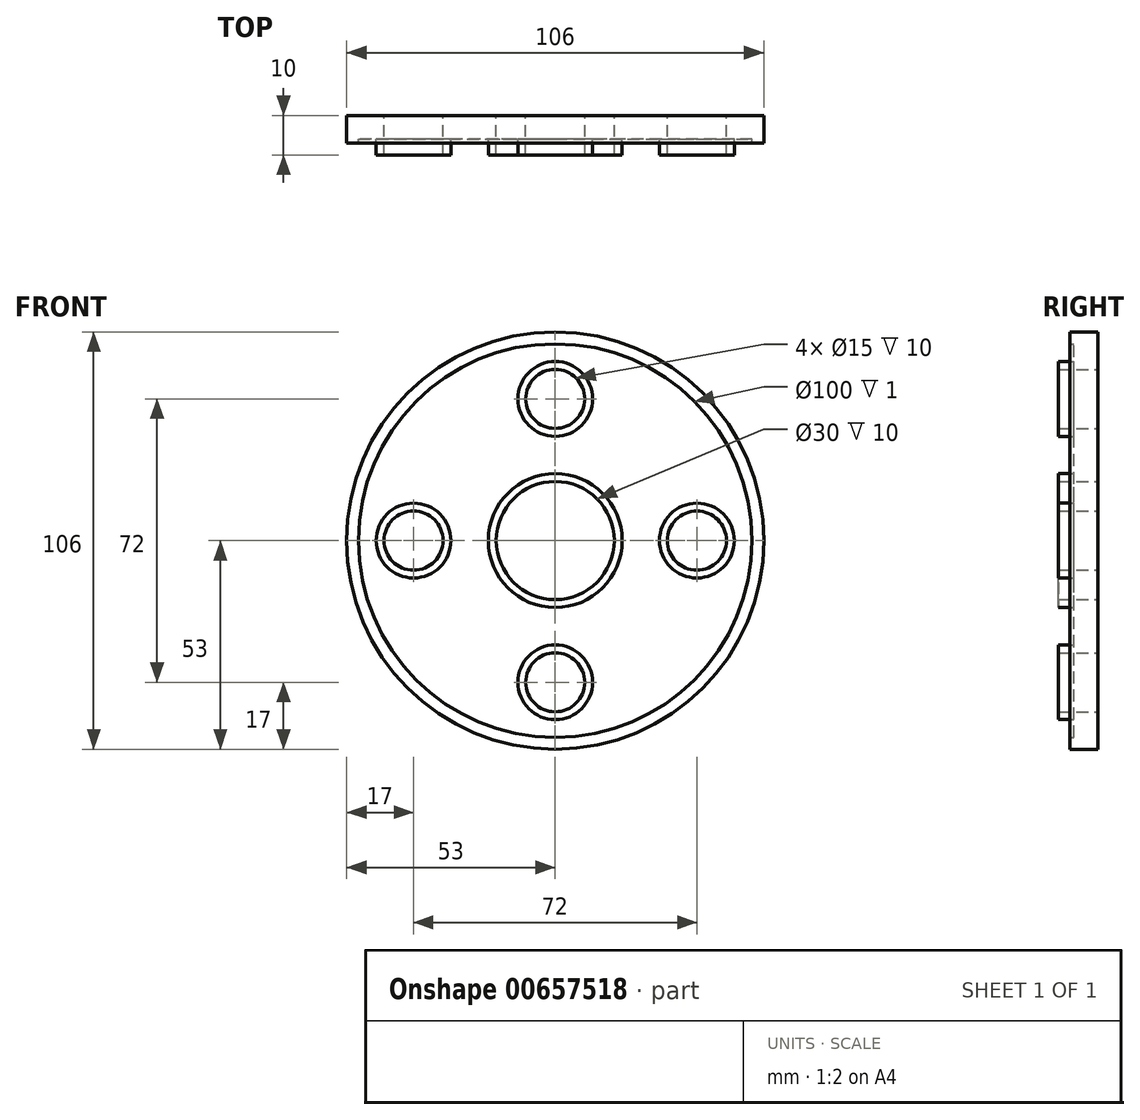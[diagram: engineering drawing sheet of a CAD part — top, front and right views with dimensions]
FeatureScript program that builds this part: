
annotation { "Feature Type Name" : "Feature", "Feature Type Description" : "" }
export const myFeature = defineFeature(function(context is Context, id is Id, definition is map)
    precondition{}
    {
        {
            var Q0;
            Q0=qCreatedBy(makeId("Front.planeOp"),FACE);
            var sketch = newSketch(context, id + "F0", { "sketchPlane" : qUnion([Q0])});
            skCircle(sketch, "E0", {"center": v(0, 0) * mm, "radius": 15 * mm});
            skCircle(sketch, "E1", {"center": v(0, 0) * mm, "radius": 50 * mm});
            skCircle(sketch, "E2", {"center": v(0, 0) * mm, "radius": 53 * mm});
            skCircle(sketch, "E3", {"center": v(0, 0) * mm, "radius": 17 * mm});
            skCircle(sketch, "E4", {"center": v(-36, 0) * mm, "radius": 7.5 * mm});
            skCircle(sketch, "E5", {"center": v(-36, 0) * mm, "radius": 9.5 * mm});
            skCircle(sketch, "E6.1.0", {"center": v(0, 36) * mm, "radius": 7.5 * mm});
            skCircle(sketch, "E6.1.1", {"center": v(0, 36) * mm, "radius": 9.5 * mm});
            skCircle(sketch, "E6.2.0", {"center": v(36, 0) * mm, "radius": 7.5 * mm});
            skCircle(sketch, "E6.2.1", {"center": v(36, 0) * mm, "radius": 9.5 * mm});
            skCircle(sketch, "E6.3.0", {"center": v(0, -36) * mm, "radius": 7.5 * mm});
            skCircle(sketch, "E6.3.1", {"center": v(0, -36) * mm, "radius": 9.5 * mm});
            skSolve(sketch);
        }
        {
            var Q0;
            Q0=makeQuery(id+"F0.imprint","IMPRINT",FACE,{"disambiguationData":[TD([[makeQuery(id+"F0.imprint","IMPRINT",EDGE,{"derivedFrom":sQuery(id+"F0.wireOp",EDGE,"E1")}),-1.0]])]});
            extrude(context, id + "F1", {"entities" : qUnion([Q0]), "depth" : 7 * mm, "offsetDistance" : 25 * mm});
        }
        {
            var Q0;
            Q0=makeQuery(id+"F0.imprint","IMPRINT",FACE,{"disambiguationData":[TD([[makeQuery(id+"F0.imprint","IMPRINT",EDGE,{"derivedFrom":sQuery(id+"F0.wireOp",EDGE,"E1")}),1.0]])]});
            extrude(context, id + "F2", {"entities" : qUnion([Q0]), "operationType" : NewBodyOperationType.ADD, "depth" : 6 * mm, "offsetDistance" : 25 * mm});
        }
        {
            var Q0;
            Q0=makeQuery(id+"F0.imprint","IMPRINT",FACE,{"disambiguationData":[TD([[makeQuery(id+"F0.imprint","IMPRINT",EDGE,{"derivedFrom":sQuery(id+"F0.wireOp",EDGE,"E6.2.0")}),-1.0]])]});
            extrude(context, id + "F3", {"entities" : qUnion([Q0]), "operationType" : NewBodyOperationType.ADD, "depth" : 10 * mm, "offsetDistance" : 25 * mm});
        }
        {
            var Q0;
            Q0=makeQuery(id+"F0.imprint","IMPRINT",FACE,{"disambiguationData":[TD([[makeQuery(id+"F0.imprint","IMPRINT",EDGE,{"derivedFrom":sQuery(id+"F0.wireOp",EDGE,"E6.1.0")}),-1.0]])]});
            extrude(context, id + "F4", {"entities" : qUnion([Q0]), "operationType" : NewBodyOperationType.ADD, "depth" : 10 * mm, "offsetDistance" : 25 * mm});
        }
        {
            var Q0;
            Q0=makeQuery(id+"F0.imprint","IMPRINT",FACE,{"disambiguationData":[TD([[makeQuery(id+"F0.imprint","IMPRINT",EDGE,{"derivedFrom":sQuery(id+"F0.wireOp",EDGE,"E0")}),-1.0]])]});
            extrude(context, id + "F5", {"entities" : qUnion([Q0]), "operationType" : NewBodyOperationType.ADD, "depth" : 10 * mm, "offsetDistance" : 25 * mm});
        }
        {
            var Q0;
            Q0=makeQuery(id+"F0.imprint","IMPRINT",FACE,{"disambiguationData":[TD([[makeQuery(id+"F0.imprint","IMPRINT",EDGE,{"derivedFrom":sQuery(id+"F0.wireOp",EDGE,"E4")}),-1.0]])]});
            extrude(context, id + "F6", {"entities" : qUnion([Q0]), "operationType" : NewBodyOperationType.ADD, "depth" : 10 * mm, "offsetDistance" : 25 * mm});
        }
        {
            var Q0;
            Q0=makeQuery(id+"F0.imprint","IMPRINT",FACE,{"disambiguationData":[TD([[makeQuery(id+"F0.imprint","IMPRINT",EDGE,{"derivedFrom":sQuery(id+"F0.wireOp",EDGE,"E6.3.0")}),-1.0]])]});
            extrude(context, id + "F7", {"entities" : qUnion([Q0]), "operationType" : NewBodyOperationType.ADD, "depth" : 10 * mm, "offsetDistance" : 25 * mm});
        }
    });
